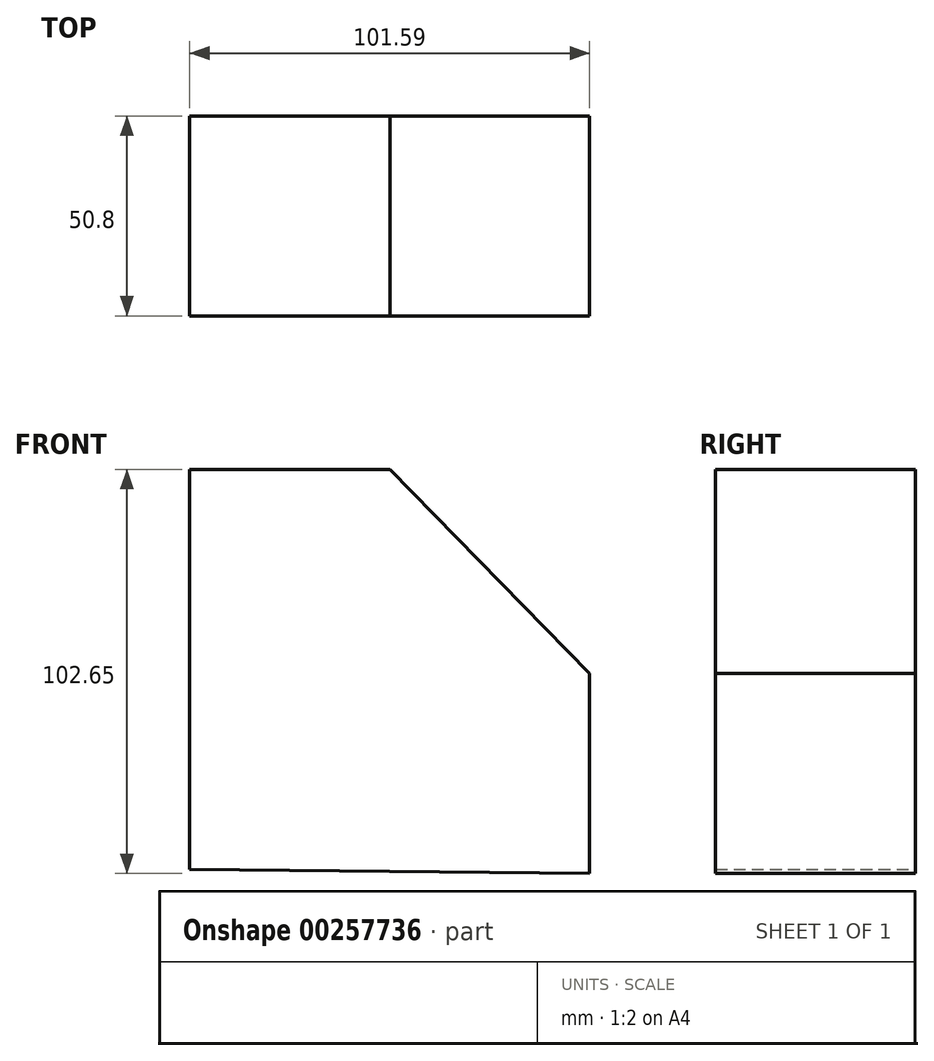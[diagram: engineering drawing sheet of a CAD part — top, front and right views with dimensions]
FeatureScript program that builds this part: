
annotation { "Feature Type Name" : "Feature", "Feature Type Description" : "" }
export const myFeature = defineFeature(function(context is Context, id is Id, definition is map)
    precondition{}
    {
        {
            var Q0;
            Q0=qCreatedBy(makeId("Front.planeOp"),FACE);
            var sketch = newSketch(context, id + "F0", { "sketchPlane" : qUnion([Q0])});
            skLineSegment(sketch, "E0", {"start": v(-23.91, 81.37) * mm, "end": v(26.89, 81.37) * mm});
            skLineSegment(sketch, "E1", {"start": v(26.89, 81.37) * mm, "end": v(77.68, 29.52) * mm});
            skLineSegment(sketch, "E2", {"start": v(77.68, 29.52) * mm, "end": v(77.68, -21.28) * mm});
            skLineSegment(sketch, "E3", {"start": v(-23.91, 81.37) * mm, "end": v(-23.91, -20.23) * mm});
            skLineSegment(sketch, "E4", {"start": v(-23.91, -20.23) * mm, "end": v(77.68, -21.28) * mm});
            skSolve(sketch);
        }
        {
            var Q0;
            Q0 = qSketchRegion(id + "F0", true);
            extrude(context, id + "F1", {"entities" : qUnion([Q0]), "depth" : 50.8 * mm});
        }
    });
